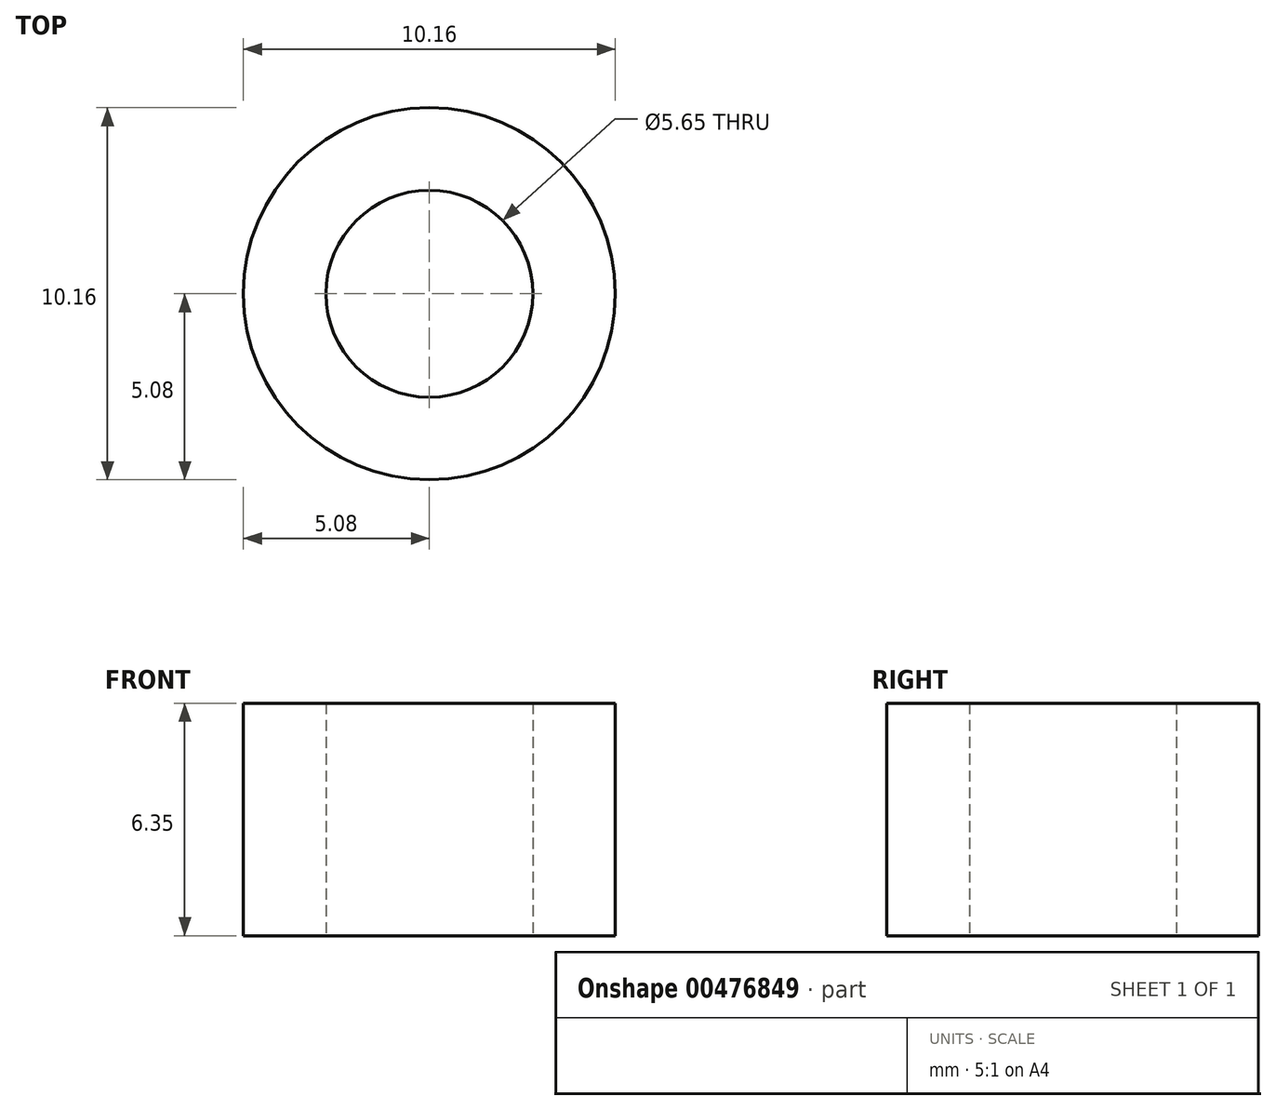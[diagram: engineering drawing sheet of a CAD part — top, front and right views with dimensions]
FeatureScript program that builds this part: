
annotation { "Feature Type Name" : "Feature", "Feature Type Description" : "" }
export const myFeature = defineFeature(function(context is Context, id is Id, definition is map)
    precondition{}
    {
        {
            var Q0;
            Q0=qCreatedBy(makeId("Top.planeOp"),FACE);
            var sketch = newSketch(context, id + "F0", { "sketchPlane" : qUnion([Q0])});
            skCircle(sketch, "E0", {"center": v(0, 0) * mm, "radius": 2.83 * mm});
            skCircle(sketch, "E1", {"center": v(0, 0) * mm, "radius": 5.08 * mm});
            skSolve(sketch);
        }
        {
            var Q0;
            Q0=makeQuery(id+"F0.imprint","IMPRINT",FACE,{"disambiguationData":[TD([[makeQuery(id+"F0.imprint","IMPRINT",EDGE,{"derivedFrom":sQuery(id+"F0.wireOp",EDGE,"E0")}),-1.0]])]});
            extrude(context, id + "F1", {"entities" : qUnion([Q0]), "depth" : 6.35 * mm});
        }
    });
